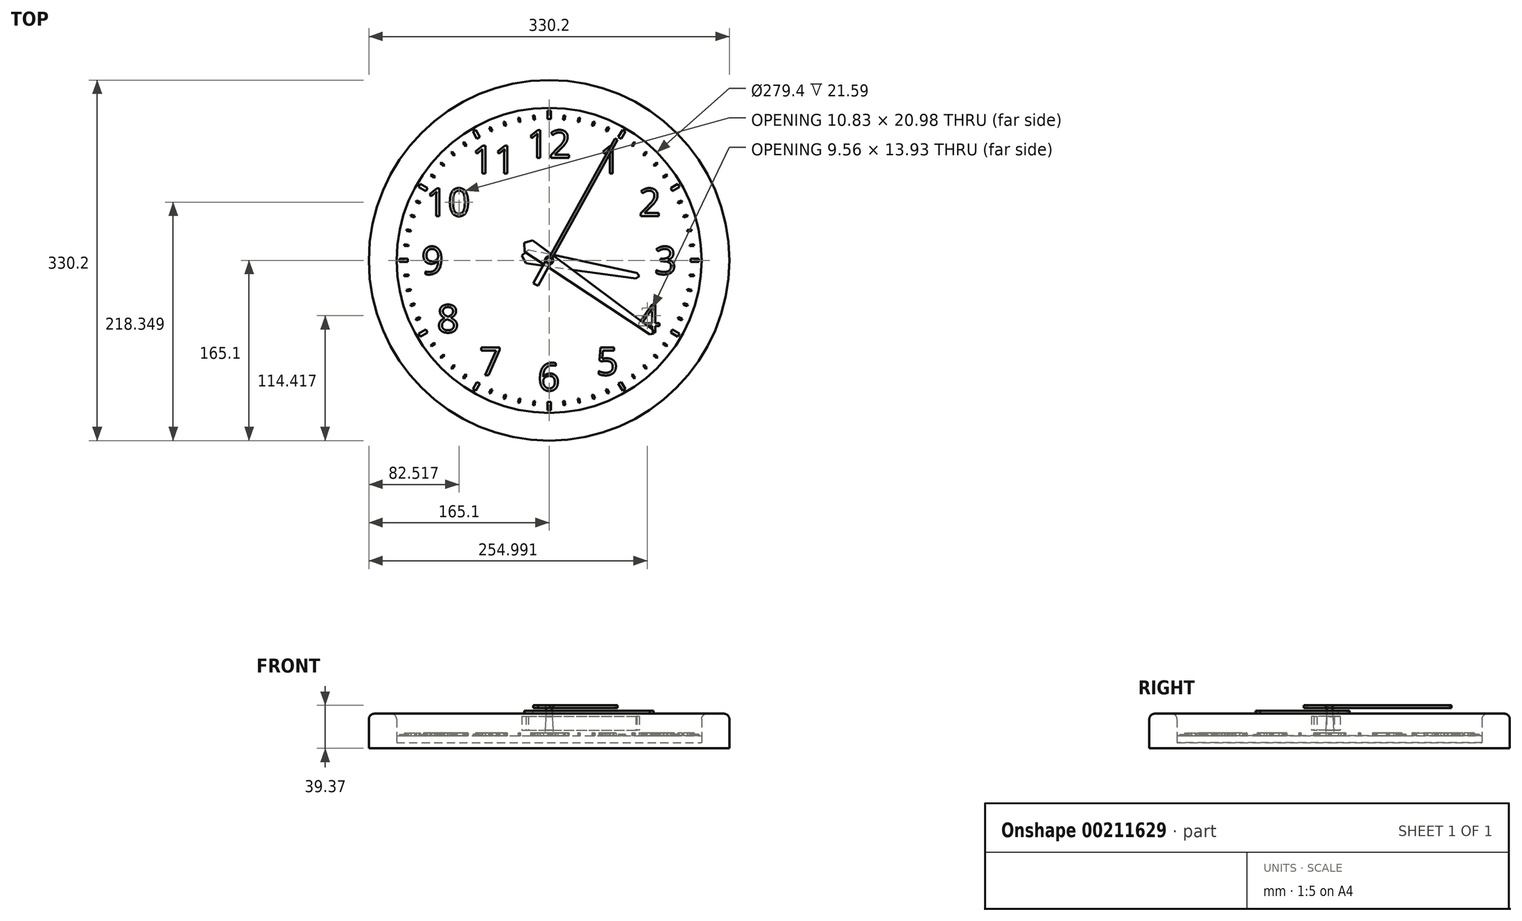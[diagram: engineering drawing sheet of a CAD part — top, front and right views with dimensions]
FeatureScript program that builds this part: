
annotation { "Feature Type Name" : "Feature", "Feature Type Description" : "" }
export const myFeature = defineFeature(function(context is Context, id is Id, definition is map)
    precondition{}
    {
        {
            var Q0;
            Q0=qCreatedBy(makeId("Front.planeOp"),FACE);
            var sketch = newSketch(context, id + "F0", { "sketchPlane" : qUnion([Q0])});
            skLineSegment(sketch, "E0", {"start": v(0, 0) * mm, "end": v(0, 54.8) * mm, "construction": true});
            skLineSegment(sketch, "E1.bottom", {"start": v(139.7, 0) * mm, "end": v(165.1, 0) * mm});
            skLineSegment(sketch, "E1.top", {"start": v(139.7, 31.75) * mm, "end": v(165.1, 31.75) * mm});
            skLineSegment(sketch, "E1.left", {"start": v(139.7, 5.08) * mm, "end": v(139.7, 31.75) * mm});
            skLineSegment(sketch, "E1.right", {"start": v(165.1, 0) * mm, "end": v(165.1, 31.75) * mm});
            skLineSegment(sketch, "E2", {"start": v(152.4, 0) * mm, "end": v(152.4, 31.75) * mm, "construction": true});
            skLineSegment(sketch, "E3.bottom", {"start": v(0, 0) * mm, "end": v(139.7, 0) * mm});
            skLineSegment(sketch, "E3.top", {"start": v(0, 5.08) * mm, "end": v(139.7, 5.08) * mm});
            skLineSegment(sketch, "E3.left", {"start": v(0, 0) * mm, "end": v(0, 5.08) * mm});
            skSolve(sketch);
        }
        {
            var Q0;
            Q0=makeQuery(id+"F0.imprint","IMPRINT",FACE,{"disambiguationData":[TD([[makeQuery(id+"F0.imprint","IMPRINT",EDGE,{"derivedFrom":sQuery(id+"F0.wireOp",EDGE,"E1.bottom")}),1.0]])]});
            var Q1;
            Q1=sQuery(id+"F0.wireOp",EDGE,"E0");
            revolve(context, id + "F1", {"entities" : qUnion([Q0]), "axis" : qUnion([Q1]), "revolveType" : RevolveType.FULL});
        }
        {
            var Q0;
            Q0=makeQuery(id+"F1.opRevolve","SWEPT_EDGE",EDGE,{"disambiguationData":[OSD([sQuery(id+"F0.wireOp",EDGE,"E1.top"),sQuery(id+"F0.wireOp",EDGE,"E1.left")])]});
            var Q1;
            Q1=makeQuery(id+"F1.opRevolve","SWEPT_EDGE",EDGE,{"disambiguationData":[OSD([sQuery(id+"F0.wireOp",EDGE,"E1.top"),sQuery(id+"F0.wireOp",EDGE,"E1.right")])]});
            fillet(context, id + "F2", {"entities" : qUnion([Q0, Q1]), "radius" : 5.08 * mm, "tangentPropagation" : true, "allowEdgeOverflow" : false});
        }
        {
            var Q0;
            Q0=makeQuery(id+"F1.opRevolve","SWEPT_FACE",FACE,{"disambiguationData":[OSD([sQuery(id+"F0.wireOp",EDGE,"E3.top")])]});
            extrude(context, id + "F3", {"entities" : qUnion([Q0]), "depth" : 6.35 * mm});
        }
        {
            var Q0;
            Q0=makeQuery(id+"F3.opExtrude","CAP_FACE",FACE,{"disambiguationData":[OSD([sQuery(id+"F0.wireOp",EDGE,"E3.top")])],"isStart":false});
            var sketch = newSketch(context, id + "F4", { "sketchPlane" : qUnion([Q0])});
            skText(sketch, "E4", { "text": "12", "fontName": "OpenSans-Regular.ttf"});
            skLineSegment(sketch, "E5", {"start": v(0, 0) * mm, "end": v(0, 106.68) * mm, "construction": true});
            skLineSegment(sketch, "E6.1.0", {"start": v(0, 0) * mm, "end": v(-53.34, 92.39) * mm, "construction": true});
            skLineSegment(sketch, "E6.2.0", {"start": v(0, 0) * mm, "end": v(-92.39, 53.34) * mm, "construction": true});
            skLineSegment(sketch, "E6.3.0", {"start": v(0, 0) * mm, "end": v(-106.68, 0) * mm, "construction": true});
            skLineSegment(sketch, "E6.4.0", {"start": v(0, 0) * mm, "end": v(-92.39, -53.34) * mm, "construction": true});
            skLineSegment(sketch, "E6.5.0", {"start": v(0, 0) * mm, "end": v(-53.34, -92.39) * mm, "construction": true});
            skLineSegment(sketch, "E6.6.0", {"start": v(0, 0) * mm, "end": v(0, -106.68) * mm, "construction": true});
            skLineSegment(sketch, "E6.7.0", {"start": v(0, 0) * mm, "end": v(53.34, -92.39) * mm, "construction": true});
            skLineSegment(sketch, "E6.8.0", {"start": v(0, 0) * mm, "end": v(92.39, -53.34) * mm, "construction": true});
            skLineSegment(sketch, "E6.9.0", {"start": v(0, 0) * mm, "end": v(106.68, 0) * mm, "construction": true});
            skLineSegment(sketch, "E6.10.0", {"start": v(0, 0) * mm, "end": v(92.39, 53.34) * mm, "construction": true});
            skLineSegment(sketch, "E6.11.0", {"start": v(0, 0) * mm, "end": v(53.34, 92.39) * mm, "construction": true});
            skPoint(sketch, "E6.center", {"position": v(0, 0) * mm});
            skText(sketch, "E7", { "text": "2", "fontName": "OpenSans-Regular.ttf"});
            skText(sketch, "E8", { "text": "3", "fontName": "OpenSans-Regular.ttf"});
            skText(sketch, "E9", { "text": "4", "fontName": "OpenSans-Regular.ttf"});
            skText(sketch, "E10", { "text": "1", "fontName": "OpenSans-Regular.ttf"});
            skText(sketch, "E11", { "text": "5", "fontName": "OpenSans-Regular.ttf"});
            skText(sketch, "E12", { "text": "6", "fontName": "OpenSans-Regular.ttf"});
            skText(sketch, "E13", { "text": "7", "fontName": "OpenSans-Regular.ttf"});
            skText(sketch, "E14", { "text": "9", "fontName": "OpenSans-Regular.ttf"});
            skText(sketch, "E15", { "text": "8", "fontName": "OpenSans-Regular.ttf"});
            skText(sketch, "E16", { "text": "10", "fontName": "OpenSans-Regular.ttf"});
            skText(sketch, "E17", { "text": "11", "fontName": "OpenSans-Regular.ttf"});
            const initialGuessF4  = {"E4": [-0.02037, 0.09398, 1, 0, 0.0254], "E7": [0.0821, 0.04064, 1, 0, 0.0254], "E8": [0.09649, -0.0127, 1, 0, 0.0254], "E9": [0.08151, -0.06604, 1, 0, 0.0254], "E10": [0.04604, 0.07969, 1, 0, 0.0254], "E11": [0.04313, -0.10509, 1, 0, 0.0254], "E12": [-0.01037, -0.11938, 1, 0, 0.0254], "E13": [-0.06367, -0.10509, 1, 0, 0.0254], "E14": [-0.11696, -0.0127, 1, 0, 0.0254], "E15": [-0.1027, -0.06604, 1, 0, 0.0254], "E16": [-0.11282, 0.04064, 1, 0, 0.0254], "E17": [-0.07073, 0.07969, 1, 0, 0.0254]};
            skSetInitialGuess(sketch, initialGuessF4);
            skSolve(sketch);
        }
        {
            var Q0;
            Q0=qSketchRegion(id+"F4",true);
            extrude(context, id + "F5", {"entities" : qUnion([Q0]), "depth" : 2.54 * mm});
        }
        {
            var Q0;
            Q0=makeQuery(id+"F3.opExtrude","CAP_FACE",FACE,{"disambiguationData":[OSD([sQuery(id+"F0.wireOp",EDGE,"E3.top")])],"isStart":false});
            cPlane(context, id + "F6", {"entities" : qUnion([Q0]), "cplaneType" : CPlaneType.OFFSET, "offset" : 5.08 * mm, "width" : 152.4 * mm, "height" : 152.4 * mm});
        }
        {
            var Q0;
            Q0=qCreatedBy(id+"F6.planeOp",FACE);
            var sketch = newSketch(context, id + "F7", { "sketchPlane" : qUnion([Q0])});
            skLineSegment(sketch, "E18", {"start": v(5, -0.88) * mm, "end": v(80.05, -14.11) * mm, "construction": true});
            skLineSegment(sketch, "E19", {"start": v(80.05, -14.11) * mm, "end": v(79.6, -16.62) * mm, "construction": true});
            skLineSegment(sketch, "E20", {"start": v(-20.01, 3.53) * mm, "end": v(-21.11, -2.72) * mm, "construction": true});
            skLineSegment(sketch, "E21", {"start": v(5, -0.88) * mm, "end": v(-25.01, 4.41) * mm, "construction": true});
            skLineSegment(sketch, "E22", {"start": v(-25.01, 4.41) * mm, "end": v(-21.11, -2.72) * mm});
            skLineSegment(sketch, "E23", {"start": v(-21.11, -2.72) * mm, "end": v(79.6, -16.62) * mm});
            skLineSegment(sketch, "E24", {"start": v(80.05, -14.11) * mm, "end": v(82.55, -14.56) * mm, "construction": true});
            skLineSegment(sketch, "E25", {"start": v(82.55, -14.56) * mm, "end": v(79.6, -16.62) * mm});
            skLineSegment(sketch, "E26.MirrorCS", {"start": v(82.55, -14.56) * mm, "end": v(80.49, -11.61) * mm});
            skLineSegment(sketch, "E27.MirrorCS", {"start": v(-18.9, 9.78) * mm, "end": v(80.49, -11.61) * mm});
            skLineSegment(sketch, "E28.MirrorCS", {"start": v(-25.01, 4.41) * mm, "end": v(-18.9, 9.78) * mm});
            skSolve(sketch);
        }
        {
            var Q0;
            Q0=makeQuery(id+"F7.imprint","IMPRINT",FACE,{"disambiguationData":[TD([[makeQuery(id+"F7.imprint","IMPRINT",EDGE,{"derivedFrom":sQuery(id+"F7.wireOp",EDGE,"E22")}),1.0]])]});
            extrude(context, id + "F8", {"entities" : qUnion([Q0]), "depth" : 12.7 * mm});
        }
        {
            var Q0;
            Q0=makeQuery(id+"F8.opExtrude","CAP_FACE",FACE,{"disambiguationData":[OSD([sQuery(id+"F7.wireOp",EDGE,"E22"),sQuery(id+"F7.wireOp",EDGE,"E23"),sQuery(id+"F7.wireOp",EDGE,"E25"),sQuery(id+"F7.wireOp",EDGE,"E26.MirrorCS"),sQuery(id+"F7.wireOp",EDGE,"E27.MirrorCS"),sQuery(id+"F7.wireOp",EDGE,"E28.MirrorCS")])],"isStart":false});
            cPlane(context, id + "F9", {"entities" : qUnion([Q0]), "cplaneType" : CPlaneType.OFFSET, "offset" : 2.54 * mm, "width" : 152.4 * mm, "height" : 152.4 * mm});
        }
        {
            var Q0;
            Q0=qCreatedBy(id+"F9.planeOp",FACE);
            var sketch = newSketch(context, id + "F10", { "sketchPlane" : qUnion([Q0])});
            skLineSegment(sketch, "E29", {"start": v(0, 0) * mm, "end": v(95.7, -67.02) * mm, "construction": true});
            skLineSegment(sketch, "E30", {"start": v(0, 0) * mm, "end": v(-22.89, 16.03) * mm, "construction": true});
            skLineSegment(sketch, "E31", {"start": v(-18.73, 13.11) * mm, "end": v(-15.08, 18.31) * mm, "construction": true});
            skLineSegment(sketch, "E32", {"start": v(93.63, -65.56) * mm, "end": v(95.09, -63.48) * mm, "construction": true});
            skLineSegment(sketch, "E33", {"start": v(-22.89, 16.03) * mm, "end": v(-15.08, 18.31) * mm});
            skLineSegment(sketch, "E34", {"start": v(-15.08, 18.31) * mm, "end": v(95.09, -63.48) * mm});
            skLineSegment(sketch, "E35", {"start": v(95.09, -63.48) * mm, "end": v(95.7, -67.02) * mm});
            skLineSegment(sketch, "E36.MirrorCS", {"start": v(-22.89, 16.03) * mm, "end": v(-22.37, 7.91) * mm});
            skLineSegment(sketch, "E37.MirrorCS", {"start": v(-22.37, 7.91) * mm, "end": v(92.17, -67.64) * mm});
            skLineSegment(sketch, "E38.MirrorCS", {"start": v(92.17, -67.64) * mm, "end": v(95.7, -67.02) * mm});
            skLineSegment(sketch, "E39", {"start": v(0, 0) * mm, "end": v(0, -35.35) * mm, "construction": true});
            skSolve(sketch);
        }
        {
            var Q0;
            Q0=makeQuery(id+"F10.imprint","IMPRINT",FACE,{"disambiguationData":[TD([[makeQuery(id+"F10.imprint","IMPRINT",EDGE,{"derivedFrom":sQuery(id+"F10.wireOp",EDGE,"E33")}),-1.0]])]});
            extrude(context, id + "F11", {"entities" : qUnion([Q0]), "depth" : 2.54 * mm});
        }
        {
            var Q0;
            Q0=makeQuery(id+"F11.opExtrude","CAP_FACE",FACE,{"disambiguationData":[OSD([sQuery(id+"F10.wireOp",EDGE,"E33"),sQuery(id+"F10.wireOp",EDGE,"E34"),sQuery(id+"F10.wireOp",EDGE,"E35"),sQuery(id+"F10.wireOp",EDGE,"E36.MirrorCS"),sQuery(id+"F10.wireOp",EDGE,"E37.MirrorCS"),sQuery(id+"F10.wireOp",EDGE,"E38.MirrorCS")])],"isStart":false});
            cPlane(context, id + "F12", {"entities" : qUnion([Q0]), "cplaneType" : CPlaneType.OFFSET, "offset" : 2.54 * mm, "width" : 152.4 * mm, "height" : 152.4 * mm});
        }
        {
            var Q0;
            Q0=qCreatedBy(id+"F12.planeOp",FACE);
            var sketch = newSketch(context, id + "F13", { "sketchPlane" : qUnion([Q0])});
            skArc(sketch, "E40", {"start": v(0.85, -3.72) * mm, "mid": v(3.63, -1.17) * mm, "end": v(2.85, 2.53) * mm});
            skLineSegment(sketch, "E41", {"start": v(0, 0) * mm, "end": v(61.55, 111.09) * mm, "construction": true});
            skLineSegment(sketch, "E42", {"start": v(0, 0) * mm, "end": v(-12.31, -22.22) * mm, "construction": true});
            skLineSegment(sketch, "E43", {"start": v(-12.31, -22.22) * mm, "end": v(-10.09, -23.45) * mm});
            skLineSegment(sketch, "E44", {"start": v(-10.09, -23.45) * mm, "end": v(0.85, -3.72) * mm});
            skLineSegment(sketch, "E45", {"start": v(61.55, 111.09) * mm, "end": v(62.66, 110.47) * mm});
            skLineSegment(sketch, "E46", {"start": v(62.66, 110.47) * mm, "end": v(2.85, 2.53) * mm});
            skLineSegment(sketch, "E47.MirrorCS", {"start": v(61.55, 111.09) * mm, "end": v(60.44, 111.7) * mm});
            skLineSegment(sketch, "E48.MirrorCS", {"start": v(60.44, 111.7) * mm, "end": v(0.63, 3.76) * mm});
            skArc(sketch, "E49.MirrorCS", {"start": v(-3.6, -1.25) * mm, "mid": v(-2.91, 2.46) * mm, "end": v(0.63, 3.76) * mm});
            skLineSegment(sketch, "E50.MirrorCS", {"start": v(-14.53, -20.99) * mm, "end": v(-3.6, -1.25) * mm});
            skLineSegment(sketch, "E51.MirrorCS", {"start": v(-12.31, -22.22) * mm, "end": v(-14.53, -20.99) * mm});
            skSolve(sketch);
        }
        {
            var Q0;
            Q0=makeQuery(id+"F13.imprint","IMPRINT",FACE,{"disambiguationData":[TD([[makeQuery(id+"F13.imprint","IMPRINT",EDGE,{"derivedFrom":sQuery(id+"F13.wireOp",EDGE,"E40")}),1.0]])]});
            extrude(context, id + "F14", {"entities" : qUnion([Q0]), "depth" : 2.54 * mm});
        }
        {
            var Q0;
            Q0=makeQuery(id+"F3.opExtrude","CAP_FACE",FACE,{"disambiguationData":[OSD([sQuery(id+"F0.wireOp",EDGE,"E3.top")])],"isStart":false});
            var sketch = newSketch(context, id + "F15", { "sketchPlane" : qUnion([Q0])});
            skCircle(sketch, "E52", {"center": v(0, 0) * mm, "radius": 3.81 * mm});
            skSolve(sketch);
        }
        {
            var Q0;
            Q0=makeQuery(id+"F14.opExtrude","CAP_FACE",FACE,{"disambiguationData":[OSD([sQuery(id+"F13.wireOp",EDGE,"E40"),sQuery(id+"F13.wireOp",EDGE,"E43"),sQuery(id+"F13.wireOp",EDGE,"E44"),sQuery(id+"F13.wireOp",EDGE,"E45"),sQuery(id+"F13.wireOp",EDGE,"E46"),sQuery(id+"F13.wireOp",EDGE,"E47.MirrorCS"),sQuery(id+"F13.wireOp",EDGE,"E48.MirrorCS"),sQuery(id+"F13.wireOp",EDGE,"E49.MirrorCS"),sQuery(id+"F13.wireOp",EDGE,"E50.MirrorCS"),sQuery(id+"F13.wireOp",EDGE,"E51.MirrorCS")])],"isStart":false});
            var sketch = newSketch(context, id + "F16", { "sketchPlane" : qUnion([Q0])});
            skCircle(sketch, "E53", {"center": v(0, 0) * mm, "radius": 2.54 * mm});
            skSolve(sketch);
        }
        {
            var Q1;
            Q1=makeQuery(id+"F15.imprint","IMPRINT",FACE,{"disambiguationData":[TD([[makeQuery(id+"F15.imprint","IMPRINT",EDGE,{"derivedFrom":sQuery(id+"F15.wireOp",EDGE,"E52")}),1.0]])]});
            var Q2;
            Q2=makeQuery(id+"F16.imprint","IMPRINT",FACE,{"disambiguationData":[TD([[makeQuery(id+"F16.imprint","IMPRINT",EDGE,{"derivedFrom":sQuery(id+"F16.wireOp",EDGE,"E53")}),1.0]])]});
            loft(context, id + "F17", {"sheetProfilesArray" : [{ "sheetProfileEntities" : qUnion([Q1]) }, { "sheetProfileEntities" : qUnion([Q2]) }]});
        }
        {
            var Q0;
            Q0=makeQuery(id+"F17.opLoft","SWEPT_BODY",BODY,{"disambiguationData":[OSD([makeQuery(id+"F15.imprint","IMPRINT",FACE,{"disambiguationData":[TD([[makeQuery(id+"F15.imprint","IMPRINT",EDGE,{"derivedFrom":sQuery(id+"F15.wireOp",EDGE,"E52")}),1.0]])]}),makeQuery(id+"F16.imprint","IMPRINT",FACE,{"disambiguationData":[TD([[makeQuery(id+"F16.imprint","IMPRINT",EDGE,{"derivedFrom":sQuery(id+"F16.wireOp",EDGE,"E53")}),1.0]])]})])]});
            var Q1;
            Q1=makeQuery(id+"F8.opExtrude","SWEPT_BODY",BODY,{"disambiguationData":[OSD([sQuery(id+"F7.wireOp",EDGE,"E22"),sQuery(id+"F7.wireOp",EDGE,"E23"),sQuery(id+"F7.wireOp",EDGE,"E25"),sQuery(id+"F7.wireOp",EDGE,"E26.MirrorCS"),sQuery(id+"F7.wireOp",EDGE,"E27.MirrorCS"),sQuery(id+"F7.wireOp",EDGE,"E28.MirrorCS")])]});
            booleanBodies(context, id + "F18", {"operationType" : BooleanOperationType.SUBTRACTION, "tools" : qUnion([Q0]), "targets" : qUnion([Q1]), "keepTools" : true});
        }
        {
            var Q0;
            Q0=makeQuery(id+"F17.opLoft","SWEPT_BODY",BODY,{"disambiguationData":[OSD([makeQuery(id+"F15.imprint","IMPRINT",FACE,{"disambiguationData":[TD([[makeQuery(id+"F15.imprint","IMPRINT",EDGE,{"derivedFrom":sQuery(id+"F15.wireOp",EDGE,"E52")}),1.0]])]}),makeQuery(id+"F16.imprint","IMPRINT",FACE,{"disambiguationData":[TD([[makeQuery(id+"F16.imprint","IMPRINT",EDGE,{"derivedFrom":sQuery(id+"F16.wireOp",EDGE,"E53")}),1.0]])]})])]});
            var Q1;
            Q1=makeQuery(id+"F11.opExtrude","SWEPT_BODY",BODY,{"disambiguationData":[OSD([sQuery(id+"F10.wireOp",EDGE,"E33"),sQuery(id+"F10.wireOp",EDGE,"E34"),sQuery(id+"F10.wireOp",EDGE,"E35"),sQuery(id+"F10.wireOp",EDGE,"E36.MirrorCS"),sQuery(id+"F10.wireOp",EDGE,"E37.MirrorCS"),sQuery(id+"F10.wireOp",EDGE,"E38.MirrorCS")])]});
            booleanBodies(context, id + "F19", {"operationType" : BooleanOperationType.SUBTRACTION, "tools" : qUnion([Q0]), "targets" : qUnion([Q1]), "keepTools" : true});
        }
        {
            var Q0;
            Q0=makeQuery(id+"F17.opLoft","SWEPT_BODY",BODY,{"disambiguationData":[OSD([makeQuery(id+"F15.imprint","IMPRINT",FACE,{"disambiguationData":[TD([[makeQuery(id+"F15.imprint","IMPRINT",EDGE,{"derivedFrom":sQuery(id+"F15.wireOp",EDGE,"E52")}),1.0]])]}),makeQuery(id+"F16.imprint","IMPRINT",FACE,{"disambiguationData":[TD([[makeQuery(id+"F16.imprint","IMPRINT",EDGE,{"derivedFrom":sQuery(id+"F16.wireOp",EDGE,"E53")}),1.0]])]})])]});
            var Q1;
            Q1=makeQuery(id+"F14.opExtrude","SWEPT_BODY",BODY,{"disambiguationData":[OSD([sQuery(id+"F13.wireOp",EDGE,"E40"),sQuery(id+"F13.wireOp",EDGE,"E43"),sQuery(id+"F13.wireOp",EDGE,"E44"),sQuery(id+"F13.wireOp",EDGE,"E45"),sQuery(id+"F13.wireOp",EDGE,"E46"),sQuery(id+"F13.wireOp",EDGE,"E47.MirrorCS"),sQuery(id+"F13.wireOp",EDGE,"E48.MirrorCS"),sQuery(id+"F13.wireOp",EDGE,"E49.MirrorCS"),sQuery(id+"F13.wireOp",EDGE,"E50.MirrorCS"),sQuery(id+"F13.wireOp",EDGE,"E51.MirrorCS")])]});
            booleanBodies(context, id + "F20", {"operationType" : BooleanOperationType.SUBTRACTION, "tools" : qUnion([Q0]), "targets" : qUnion([Q1]), "keepTools" : true});
        }
        {
            var Q0;
            Q0=makeQuery(id+"F18.opBoolean","INTERSECT",EDGE,{"derivedFrom":[makeQuery(id+"F17.opLoft","SWEPT_FACE",FACE,{"disambiguationData":[OSD([sQuery(id+"F15.wireOp",EDGE,"E52"),sQuery(id+"F16.wireOp",EDGE,"E53")])]}),makeQuery(id+"F8.opExtrude","CAP_FACE",FACE,{"disambiguationData":[OSD([sQuery(id+"F7.wireOp",EDGE,"E22"),sQuery(id+"F7.wireOp",EDGE,"E23"),sQuery(id+"F7.wireOp",EDGE,"E25"),sQuery(id+"F7.wireOp",EDGE,"E26.MirrorCS"),sQuery(id+"F7.wireOp",EDGE,"E27.MirrorCS"),sQuery(id+"F7.wireOp",EDGE,"E28.MirrorCS")])],"isStart":true})]});
            var Q1;
            Q1=makeQuery(id+"F18.opBoolean","INTERSECT",EDGE,{"derivedFrom":[makeQuery(id+"F17.opLoft","SWEPT_FACE",FACE,{"disambiguationData":[OSD([sQuery(id+"F15.wireOp",EDGE,"E52"),sQuery(id+"F16.wireOp",EDGE,"E53")])]}),makeQuery(id+"F8.opExtrude","CAP_FACE",FACE,{"disambiguationData":[OSD([sQuery(id+"F7.wireOp",EDGE,"E22"),sQuery(id+"F7.wireOp",EDGE,"E23"),sQuery(id+"F7.wireOp",EDGE,"E25"),sQuery(id+"F7.wireOp",EDGE,"E26.MirrorCS"),sQuery(id+"F7.wireOp",EDGE,"E27.MirrorCS"),sQuery(id+"F7.wireOp",EDGE,"E28.MirrorCS")])],"isStart":false})]});
            var Q2;
            Q2=makeQuery(id+"F19.opBoolean","INTERSECT",EDGE,{"derivedFrom":[makeQuery(id+"F17.opLoft","SWEPT_FACE",FACE,{"disambiguationData":[OSD([sQuery(id+"F15.wireOp",EDGE,"E52"),sQuery(id+"F16.wireOp",EDGE,"E53")])]}),makeQuery(id+"F11.opExtrude","CAP_FACE",FACE,{"disambiguationData":[OSD([sQuery(id+"F10.wireOp",EDGE,"E33"),sQuery(id+"F10.wireOp",EDGE,"E34"),sQuery(id+"F10.wireOp",EDGE,"E35"),sQuery(id+"F10.wireOp",EDGE,"E36.MirrorCS"),sQuery(id+"F10.wireOp",EDGE,"E37.MirrorCS"),sQuery(id+"F10.wireOp",EDGE,"E38.MirrorCS")])],"isStart":true})]});
            var Q3;
            Q3=makeQuery(id+"F19.opBoolean","INTERSECT",EDGE,{"derivedFrom":[makeQuery(id+"F17.opLoft","SWEPT_FACE",FACE,{"disambiguationData":[OSD([sQuery(id+"F15.wireOp",EDGE,"E52"),sQuery(id+"F16.wireOp",EDGE,"E53")])]}),makeQuery(id+"F11.opExtrude","CAP_FACE",FACE,{"disambiguationData":[OSD([sQuery(id+"F10.wireOp",EDGE,"E33"),sQuery(id+"F10.wireOp",EDGE,"E34"),sQuery(id+"F10.wireOp",EDGE,"E35"),sQuery(id+"F10.wireOp",EDGE,"E36.MirrorCS"),sQuery(id+"F10.wireOp",EDGE,"E37.MirrorCS"),sQuery(id+"F10.wireOp",EDGE,"E38.MirrorCS")])],"isStart":false})]});
            var Q4;
            Q4=makeQuery(id+"F20.opBoolean","INTERSECT",EDGE,{"derivedFrom":[makeQuery(id+"F17.opLoft","SWEPT_FACE",FACE,{"disambiguationData":[OSD([sQuery(id+"F15.wireOp",EDGE,"E52"),sQuery(id+"F16.wireOp",EDGE,"E53")])]}),makeQuery(id+"F14.opExtrude","CAP_FACE",FACE,{"disambiguationData":[OSD([sQuery(id+"F13.wireOp",EDGE,"E40"),sQuery(id+"F13.wireOp",EDGE,"E43"),sQuery(id+"F13.wireOp",EDGE,"E44"),sQuery(id+"F13.wireOp",EDGE,"E45"),sQuery(id+"F13.wireOp",EDGE,"E46"),sQuery(id+"F13.wireOp",EDGE,"E47.MirrorCS"),sQuery(id+"F13.wireOp",EDGE,"E48.MirrorCS"),sQuery(id+"F13.wireOp",EDGE,"E49.MirrorCS"),sQuery(id+"F13.wireOp",EDGE,"E50.MirrorCS"),sQuery(id+"F13.wireOp",EDGE,"E51.MirrorCS")])],"isStart":true})]});
            var Q5;
            Q5=makeQuery(id+"F20.opBoolean","COPY",EDGE,{"derivedFrom":makeQuery(id+"F17.opLoft","MID_CAP_EDGE",EDGE,{"disambiguationData":[OSD([sQuery(id+"F15.wireOp",EDGE,"E52"),sQuery(id+"F16.wireOp",EDGE,"E53")])],"capPos":1.0})});
            chamfer(context, id + "F21", {"entities" : qUnion([Q0, Q1, Q2, Q3, Q4, Q5]), "width" : 0.25 * mm, "tangentPropagation" : true});
        }
        {
            var Q0;
            Q0=makeQuery(id+"F3.opExtrude","CAP_FACE",FACE,{"disambiguationData":[OSD([sQuery(id+"F0.wireOp",EDGE,"E3.top")])],"isStart":false});
            var sketch = newSketch(context, id + "F22", { "sketchPlane" : qUnion([Q0])});
            skLineSegment(sketch, "E54", {"start": v(0, 0) * mm, "end": v(0, 139.7) * mm, "construction": true});
            skLineSegment(sketch, "E55.bottom", {"start": v(1.52, 137.16) * mm, "end": v(-1.52, 137.16) * mm});
            skLineSegment(sketch, "E55.top", {"start": v(1.52, 129.54) * mm, "end": v(-1.52, 129.54) * mm});
            skLineSegment(sketch, "E55.left", {"start": v(1.52, 137.16) * mm, "end": v(1.52, 129.54) * mm});
            skLineSegment(sketch, "E55.right", {"start": v(-1.52, 137.16) * mm, "end": v(-1.52, 129.54) * mm});
            skPoint(sketch, "E55.middle", {"position": v(0, 133.35) * mm});
            skSolve(sketch);
        }
        {
            var Q0;
            Q0=makeQuery(id+"F22.imprint","IMPRINT",FACE,{"disambiguationData":[TD([[makeQuery(id+"F22.imprint","IMPRINT",EDGE,{"derivedFrom":sQuery(id+"F22.wireOp",EDGE,"E55.bottom")}),1.0]])]});
            extrude(context, id + "F23", {"entities" : qUnion([Q0]), "depth" : 1.27 * mm});
        }
        {
            var Q0;
            Q0=makeQuery(id+"F23.opExtrude","SWEPT_BODY",BODY,{"disambiguationData":[OSD([sQuery(id+"F22.wireOp",EDGE,"E55.bottom"),sQuery(id+"F22.wireOp",EDGE,"E55.top"),sQuery(id+"F22.wireOp",EDGE,"E55.left"),sQuery(id+"F22.wireOp",EDGE,"E55.right")])]});
            var Q1;
            Q1=sQuery(id+"F0.wireOp",EDGE,"E0");
            circularPattern(context, id + "F24", {"entities" : qUnion([Q0]), "axis" : qUnion([Q1]), "angle" : 360 * degree, "instanceCount" : 12, "equalSpace" : true});
        }
        {
            var Q0;
            Q0=makeQuery(id+"F3.opExtrude","CAP_FACE",FACE,{"disambiguationData":[OSD([sQuery(id+"F0.wireOp",EDGE,"E3.top")])],"isStart":false});
            var sketch = newSketch(context, id + "F25", { "sketchPlane" : qUnion([Q0])});
            skLineSegment(sketch, "E56", {"start": v(0, 0) * mm, "end": v(0, 65.46) * mm, "construction": true});
            skLineSegment(sketch, "E57", {"start": v(0, 0) * mm, "end": v(13.94, 132.62) * mm, "construction": true});
            skLineSegment(sketch, "E58", {"start": v(13.54, 128.83) * mm, "end": v(14.3, 128.75) * mm});
            skLineSegment(sketch, "E59", {"start": v(13.94, 132.62) * mm, "end": v(14.7, 132.54) * mm});
            skLineSegment(sketch, "E60", {"start": v(14.7, 132.54) * mm, "end": v(14.3, 128.75) * mm});
            skLineSegment(sketch, "E61.MirrorCS", {"start": v(13.94, 132.62) * mm, "end": v(13.18, 132.7) * mm});
            skLineSegment(sketch, "E62.MirrorCS", {"start": v(13.18, 132.7) * mm, "end": v(12.78, 128.91) * mm});
            skLineSegment(sketch, "E63.MirrorCS", {"start": v(13.54, 128.83) * mm, "end": v(12.78, 128.91) * mm});
            skLineSegment(sketch, "E64.2.0", {"start": v(-13.18, 132.7) * mm, "end": v(-12.78, 128.91) * mm});
            skLineSegment(sketch, "E64.2.1", {"start": v(-13.94, 132.62) * mm, "end": v(-13.18, 132.7) * mm});
            skLineSegment(sketch, "E64.2.2", {"start": v(-13.94, 132.62) * mm, "end": v(-14.7, 132.54) * mm});
            skLineSegment(sketch, "E64.2.3", {"start": v(-14.7, 132.54) * mm, "end": v(-14.3, 128.75) * mm});
            skLineSegment(sketch, "E64.2.4", {"start": v(-13.54, 128.83) * mm, "end": v(-14.3, 128.75) * mm});
            skLineSegment(sketch, "E64.2.5", {"start": v(-13.54, 128.83) * mm, "end": v(-12.78, 128.91) * mm});
            skLineSegment(sketch, "E64.3.0", {"start": v(-26.98, 130.6) * mm, "end": v(-26.19, 126.87) * mm});
            skLineSegment(sketch, "E64.3.1", {"start": v(-27.73, 130.44) * mm, "end": v(-26.98, 130.6) * mm});
            skLineSegment(sketch, "E64.3.2", {"start": v(-27.73, 130.44) * mm, "end": v(-28.47, 130.28) * mm});
            skLineSegment(sketch, "E64.3.3", {"start": v(-28.47, 130.28) * mm, "end": v(-27.68, 126.55) * mm});
            skLineSegment(sketch, "E64.3.4", {"start": v(-26.93, 126.7) * mm, "end": v(-27.68, 126.55) * mm});
            skLineSegment(sketch, "E64.3.5", {"start": v(-26.93, 126.7) * mm, "end": v(-26.19, 126.87) * mm});
            skLineSegment(sketch, "E64.4.0", {"start": v(-40.48, 127.06) * mm, "end": v(-39.3, 123.44) * mm});
            skLineSegment(sketch, "E64.4.1", {"start": v(-41.2, 126.82) * mm, "end": v(-40.48, 127.06) * mm});
            skLineSegment(sketch, "E64.4.2", {"start": v(-41.2, 126.82) * mm, "end": v(-41.93, 126.59) * mm});
            skLineSegment(sketch, "E64.4.3", {"start": v(-41.93, 126.59) * mm, "end": v(-40.75, 122.96) * mm});
            skLineSegment(sketch, "E64.4.4", {"start": v(-40.03, 123.2) * mm, "end": v(-40.75, 122.96) * mm});
            skLineSegment(sketch, "E64.4.5", {"start": v(-40.03, 123.2) * mm, "end": v(-39.3, 123.44) * mm});
            skLineSegment(sketch, "E64.5.0", {"start": v(-53.54, 122.13) * mm, "end": v(-52, 118.65) * mm});
            skLineSegment(sketch, "E64.5.1", {"start": v(-54.24, 121.82) * mm, "end": v(-53.54, 122.13) * mm});
            skLineSegment(sketch, "E64.5.2", {"start": v(-54.24, 121.82) * mm, "end": v(-54.93, 121.51) * mm});
            skLineSegment(sketch, "E64.5.3", {"start": v(-54.93, 121.51) * mm, "end": v(-53.38, 118.03) * mm});
            skLineSegment(sketch, "E64.5.4", {"start": v(-52.69, 118.34) * mm, "end": v(-53.38, 118.03) * mm});
            skLineSegment(sketch, "E64.5.5", {"start": v(-52.69, 118.34) * mm, "end": v(-52, 118.65) * mm});
            skLineSegment(sketch, "E64.7.0", {"start": v(-77.76, 108.33) * mm, "end": v(-75.53, 105.25) * mm});
            skLineSegment(sketch, "E64.7.1", {"start": v(-78.38, 107.88) * mm, "end": v(-77.76, 108.33) * mm});
            skLineSegment(sketch, "E64.7.2", {"start": v(-78.38, 107.88) * mm, "end": v(-79, 107.43) * mm});
            skLineSegment(sketch, "E64.7.3", {"start": v(-79, 107.43) * mm, "end": v(-76.76, 104.35) * mm});
            skLineSegment(sketch, "E64.7.4", {"start": v(-76.14, 104.8) * mm, "end": v(-76.76, 104.35) * mm});
            skLineSegment(sketch, "E64.7.5", {"start": v(-76.14, 104.8) * mm, "end": v(-75.53, 105.25) * mm});
            skLineSegment(sketch, "E64.8.0", {"start": v(-88.66, 99.6) * mm, "end": v(-86.11, 96.78) * mm});
            skLineSegment(sketch, "E64.8.1", {"start": v(-89.23, 99.1) * mm, "end": v(-88.66, 99.6) * mm});
            skLineSegment(sketch, "E64.8.2", {"start": v(-89.23, 99.1) * mm, "end": v(-89.8, 98.59) * mm});
            skLineSegment(sketch, "E64.8.3", {"start": v(-89.8, 98.59) * mm, "end": v(-87.25, 95.76) * mm});
            skLineSegment(sketch, "E64.8.4", {"start": v(-86.68, 96.27) * mm, "end": v(-87.25, 95.76) * mm});
            skLineSegment(sketch, "E64.8.5", {"start": v(-86.68, 96.27) * mm, "end": v(-86.11, 96.78) * mm});
            skLineSegment(sketch, "E64.9.0", {"start": v(-98.59, 89.8) * mm, "end": v(-95.76, 87.25) * mm});
            skLineSegment(sketch, "E64.9.1", {"start": v(-99.1, 89.23) * mm, "end": v(-98.59, 89.8) * mm});
            skLineSegment(sketch, "E64.9.2", {"start": v(-99.1, 89.23) * mm, "end": v(-99.6, 88.66) * mm});
            skLineSegment(sketch, "E64.9.3", {"start": v(-99.6, 88.66) * mm, "end": v(-96.78, 86.11) * mm});
            skLineSegment(sketch, "E64.9.4", {"start": v(-96.27, 86.68) * mm, "end": v(-96.78, 86.11) * mm});
            skLineSegment(sketch, "E64.9.5", {"start": v(-96.27, 86.68) * mm, "end": v(-95.76, 87.25) * mm});
            skLineSegment(sketch, "E64.10.0", {"start": v(-107.43, 79) * mm, "end": v(-104.35, 76.76) * mm});
            skLineSegment(sketch, "E64.10.1", {"start": v(-107.88, 78.38) * mm, "end": v(-107.43, 79) * mm});
            skLineSegment(sketch, "E64.10.2", {"start": v(-107.88, 78.38) * mm, "end": v(-108.33, 77.76) * mm});
            skLineSegment(sketch, "E64.10.3", {"start": v(-108.33, 77.76) * mm, "end": v(-105.25, 75.53) * mm});
            skLineSegment(sketch, "E64.10.4", {"start": v(-104.8, 76.14) * mm, "end": v(-105.25, 75.53) * mm});
            skLineSegment(sketch, "E64.10.5", {"start": v(-104.8, 76.14) * mm, "end": v(-104.35, 76.76) * mm});
            skLineSegment(sketch, "E64.12.0", {"start": v(-121.51, 54.93) * mm, "end": v(-118.03, 53.38) * mm});
            skLineSegment(sketch, "E64.12.1", {"start": v(-121.82, 54.24) * mm, "end": v(-121.51, 54.93) * mm});
            skLineSegment(sketch, "E64.12.2", {"start": v(-121.82, 54.24) * mm, "end": v(-122.13, 53.54) * mm});
            skLineSegment(sketch, "E64.12.3", {"start": v(-122.13, 53.54) * mm, "end": v(-118.65, 52) * mm});
            skLineSegment(sketch, "E64.12.4", {"start": v(-118.34, 52.69) * mm, "end": v(-118.65, 52) * mm});
            skLineSegment(sketch, "E64.12.5", {"start": v(-118.34, 52.69) * mm, "end": v(-118.03, 53.38) * mm});
            skLineSegment(sketch, "E64.13.0", {"start": v(-126.59, 41.93) * mm, "end": v(-122.96, 40.75) * mm});
            skLineSegment(sketch, "E64.13.1", {"start": v(-126.82, 41.2) * mm, "end": v(-126.59, 41.93) * mm});
            skLineSegment(sketch, "E64.13.2", {"start": v(-126.82, 41.2) * mm, "end": v(-127.06, 40.48) * mm});
            skLineSegment(sketch, "E64.13.3", {"start": v(-127.06, 40.48) * mm, "end": v(-123.44, 39.3) * mm});
            skLineSegment(sketch, "E64.13.4", {"start": v(-123.2, 40.03) * mm, "end": v(-123.44, 39.3) * mm});
            skLineSegment(sketch, "E64.13.5", {"start": v(-123.2, 40.03) * mm, "end": v(-122.96, 40.75) * mm});
            skLineSegment(sketch, "E64.14.0", {"start": v(-130.28, 28.47) * mm, "end": v(-126.55, 27.68) * mm});
            skLineSegment(sketch, "E64.14.1", {"start": v(-130.44, 27.73) * mm, "end": v(-130.28, 28.47) * mm});
            skLineSegment(sketch, "E64.14.2", {"start": v(-130.44, 27.73) * mm, "end": v(-130.6, 26.98) * mm});
            skLineSegment(sketch, "E64.14.3", {"start": v(-130.6, 26.98) * mm, "end": v(-126.87, 26.19) * mm});
            skLineSegment(sketch, "E64.14.4", {"start": v(-126.7, 26.93) * mm, "end": v(-126.87, 26.19) * mm});
            skLineSegment(sketch, "E64.14.5", {"start": v(-126.7, 26.93) * mm, "end": v(-126.55, 27.68) * mm});
            skLineSegment(sketch, "E64.15.0", {"start": v(-132.54, 14.7) * mm, "end": v(-128.75, 14.3) * mm});
            skLineSegment(sketch, "E64.15.1", {"start": v(-132.62, 13.94) * mm, "end": v(-132.54, 14.7) * mm});
            skLineSegment(sketch, "E64.15.2", {"start": v(-132.62, 13.94) * mm, "end": v(-132.7, 13.18) * mm});
            skLineSegment(sketch, "E64.15.3", {"start": v(-132.7, 13.18) * mm, "end": v(-128.91, 12.78) * mm});
            skLineSegment(sketch, "E64.15.4", {"start": v(-128.83, 13.54) * mm, "end": v(-128.91, 12.78) * mm});
            skLineSegment(sketch, "E64.15.5", {"start": v(-128.83, 13.54) * mm, "end": v(-128.75, 14.3) * mm});
            skLineSegment(sketch, "E64.17.0", {"start": v(-132.7, -13.18) * mm, "end": v(-128.91, -12.78) * mm});
            skLineSegment(sketch, "E64.17.1", {"start": v(-132.62, -13.94) * mm, "end": v(-132.7, -13.18) * mm});
            skLineSegment(sketch, "E64.17.2", {"start": v(-132.62, -13.94) * mm, "end": v(-132.54, -14.7) * mm});
            skLineSegment(sketch, "E64.17.3", {"start": v(-132.54, -14.7) * mm, "end": v(-128.75, -14.3) * mm});
            skLineSegment(sketch, "E64.17.4", {"start": v(-128.83, -13.54) * mm, "end": v(-128.75, -14.3) * mm});
            skLineSegment(sketch, "E64.17.5", {"start": v(-128.83, -13.54) * mm, "end": v(-128.91, -12.78) * mm});
            skLineSegment(sketch, "E64.18.0", {"start": v(-130.6, -26.98) * mm, "end": v(-126.87, -26.19) * mm});
            skLineSegment(sketch, "E64.18.1", {"start": v(-130.44, -27.73) * mm, "end": v(-130.6, -26.98) * mm});
            skLineSegment(sketch, "E64.18.2", {"start": v(-130.44, -27.73) * mm, "end": v(-130.28, -28.47) * mm});
            skLineSegment(sketch, "E64.18.3", {"start": v(-130.28, -28.47) * mm, "end": v(-126.55, -27.68) * mm});
            skLineSegment(sketch, "E64.18.4", {"start": v(-126.7, -26.93) * mm, "end": v(-126.55, -27.68) * mm});
            skLineSegment(sketch, "E64.18.5", {"start": v(-126.7, -26.93) * mm, "end": v(-126.87, -26.19) * mm});
            skLineSegment(sketch, "E64.19.0", {"start": v(-127.06, -40.48) * mm, "end": v(-123.44, -39.3) * mm});
            skLineSegment(sketch, "E64.19.1", {"start": v(-126.82, -41.2) * mm, "end": v(-127.06, -40.48) * mm});
            skLineSegment(sketch, "E64.19.2", {"start": v(-126.82, -41.2) * mm, "end": v(-126.59, -41.93) * mm});
            skLineSegment(sketch, "E64.19.3", {"start": v(-126.59, -41.93) * mm, "end": v(-122.96, -40.75) * mm});
            skLineSegment(sketch, "E64.19.4", {"start": v(-123.2, -40.03) * mm, "end": v(-122.96, -40.75) * mm});
            skLineSegment(sketch, "E64.19.5", {"start": v(-123.2, -40.03) * mm, "end": v(-123.44, -39.3) * mm});
            skLineSegment(sketch, "E64.20.0", {"start": v(-122.13, -53.54) * mm, "end": v(-118.65, -52) * mm});
            skLineSegment(sketch, "E64.20.1", {"start": v(-121.82, -54.24) * mm, "end": v(-122.13, -53.54) * mm});
            skLineSegment(sketch, "E64.20.2", {"start": v(-121.82, -54.24) * mm, "end": v(-121.51, -54.93) * mm});
            skLineSegment(sketch, "E64.20.3", {"start": v(-121.51, -54.93) * mm, "end": v(-118.03, -53.38) * mm});
            skLineSegment(sketch, "E64.20.4", {"start": v(-118.34, -52.69) * mm, "end": v(-118.03, -53.38) * mm});
            skLineSegment(sketch, "E64.20.5", {"start": v(-118.34, -52.69) * mm, "end": v(-118.65, -52) * mm});
            skLineSegment(sketch, "E64.22.0", {"start": v(-108.33, -77.76) * mm, "end": v(-105.25, -75.53) * mm});
            skLineSegment(sketch, "E64.22.1", {"start": v(-107.88, -78.38) * mm, "end": v(-108.33, -77.76) * mm});
            skLineSegment(sketch, "E64.22.2", {"start": v(-107.88, -78.38) * mm, "end": v(-107.43, -79) * mm});
            skLineSegment(sketch, "E64.22.3", {"start": v(-107.43, -79) * mm, "end": v(-104.35, -76.76) * mm});
            skLineSegment(sketch, "E64.22.4", {"start": v(-104.8, -76.14) * mm, "end": v(-104.35, -76.76) * mm});
            skLineSegment(sketch, "E64.22.5", {"start": v(-104.8, -76.14) * mm, "end": v(-105.25, -75.53) * mm});
            skLineSegment(sketch, "E64.23.0", {"start": v(-99.6, -88.66) * mm, "end": v(-96.78, -86.11) * mm});
            skLineSegment(sketch, "E64.23.1", {"start": v(-99.1, -89.23) * mm, "end": v(-99.6, -88.66) * mm});
            skLineSegment(sketch, "E64.23.2", {"start": v(-99.1, -89.23) * mm, "end": v(-98.59, -89.8) * mm});
            skLineSegment(sketch, "E64.23.3", {"start": v(-98.59, -89.8) * mm, "end": v(-95.76, -87.25) * mm});
            skLineSegment(sketch, "E64.23.4", {"start": v(-96.27, -86.68) * mm, "end": v(-95.76, -87.25) * mm});
            skLineSegment(sketch, "E64.23.5", {"start": v(-96.27, -86.68) * mm, "end": v(-96.78, -86.11) * mm});
            skLineSegment(sketch, "E64.24.0", {"start": v(-89.8, -98.59) * mm, "end": v(-87.25, -95.76) * mm});
            skLineSegment(sketch, "E64.24.1", {"start": v(-89.23, -99.1) * mm, "end": v(-89.8, -98.59) * mm});
            skLineSegment(sketch, "E64.24.2", {"start": v(-89.23, -99.1) * mm, "end": v(-88.66, -99.6) * mm});
            skLineSegment(sketch, "E64.24.3", {"start": v(-88.66, -99.6) * mm, "end": v(-86.11, -96.78) * mm});
            skLineSegment(sketch, "E64.24.4", {"start": v(-86.68, -96.27) * mm, "end": v(-86.11, -96.78) * mm});
            skLineSegment(sketch, "E64.24.5", {"start": v(-86.68, -96.27) * mm, "end": v(-87.25, -95.76) * mm});
            skLineSegment(sketch, "E64.25.0", {"start": v(-79, -107.43) * mm, "end": v(-76.76, -104.35) * mm});
            skLineSegment(sketch, "E64.25.1", {"start": v(-78.38, -107.88) * mm, "end": v(-79, -107.43) * mm});
            skLineSegment(sketch, "E64.25.2", {"start": v(-78.38, -107.88) * mm, "end": v(-77.76, -108.33) * mm});
            skLineSegment(sketch, "E64.25.3", {"start": v(-77.76, -108.33) * mm, "end": v(-75.53, -105.25) * mm});
            skLineSegment(sketch, "E64.25.4", {"start": v(-76.14, -104.8) * mm, "end": v(-75.53, -105.25) * mm});
            skLineSegment(sketch, "E64.25.5", {"start": v(-76.14, -104.8) * mm, "end": v(-76.76, -104.35) * mm});
            skLineSegment(sketch, "E64.27.0", {"start": v(-54.93, -121.51) * mm, "end": v(-53.38, -118.03) * mm});
            skLineSegment(sketch, "E64.27.1", {"start": v(-54.24, -121.82) * mm, "end": v(-54.93, -121.51) * mm});
            skLineSegment(sketch, "E64.27.2", {"start": v(-54.24, -121.82) * mm, "end": v(-53.54, -122.13) * mm});
            skLineSegment(sketch, "E64.27.3", {"start": v(-53.54, -122.13) * mm, "end": v(-52, -118.65) * mm});
            skLineSegment(sketch, "E64.27.4", {"start": v(-52.69, -118.34) * mm, "end": v(-52, -118.65) * mm});
            skLineSegment(sketch, "E64.27.5", {"start": v(-52.69, -118.34) * mm, "end": v(-53.38, -118.03) * mm});
            skLineSegment(sketch, "E64.28.0", {"start": v(-41.93, -126.59) * mm, "end": v(-40.75, -122.96) * mm});
            skLineSegment(sketch, "E64.28.1", {"start": v(-41.2, -126.82) * mm, "end": v(-41.93, -126.59) * mm});
            skLineSegment(sketch, "E64.28.2", {"start": v(-41.2, -126.82) * mm, "end": v(-40.48, -127.06) * mm});
            skLineSegment(sketch, "E64.28.3", {"start": v(-40.48, -127.06) * mm, "end": v(-39.3, -123.44) * mm});
            skLineSegment(sketch, "E64.28.4", {"start": v(-40.03, -123.2) * mm, "end": v(-39.3, -123.44) * mm});
            skLineSegment(sketch, "E64.28.5", {"start": v(-40.03, -123.2) * mm, "end": v(-40.75, -122.96) * mm});
            skLineSegment(sketch, "E64.29.0", {"start": v(-28.47, -130.28) * mm, "end": v(-27.68, -126.55) * mm});
            skLineSegment(sketch, "E64.29.1", {"start": v(-27.73, -130.44) * mm, "end": v(-28.47, -130.28) * mm});
            skLineSegment(sketch, "E64.29.2", {"start": v(-27.73, -130.44) * mm, "end": v(-26.98, -130.6) * mm});
            skLineSegment(sketch, "E64.29.3", {"start": v(-26.98, -130.6) * mm, "end": v(-26.19, -126.87) * mm});
            skLineSegment(sketch, "E64.29.4", {"start": v(-26.93, -126.7) * mm, "end": v(-26.19, -126.87) * mm});
            skLineSegment(sketch, "E64.29.5", {"start": v(-26.93, -126.7) * mm, "end": v(-27.68, -126.55) * mm});
            skLineSegment(sketch, "E64.30.0", {"start": v(-14.7, -132.54) * mm, "end": v(-14.3, -128.75) * mm});
            skLineSegment(sketch, "E64.30.1", {"start": v(-13.94, -132.62) * mm, "end": v(-14.7, -132.54) * mm});
            skLineSegment(sketch, "E64.30.2", {"start": v(-13.94, -132.62) * mm, "end": v(-13.18, -132.7) * mm});
            skLineSegment(sketch, "E64.30.3", {"start": v(-13.18, -132.7) * mm, "end": v(-12.78, -128.91) * mm});
            skLineSegment(sketch, "E64.30.4", {"start": v(-13.54, -128.83) * mm, "end": v(-12.78, -128.91) * mm});
            skLineSegment(sketch, "E64.30.5", {"start": v(-13.54, -128.83) * mm, "end": v(-14.3, -128.75) * mm});
            skLineSegment(sketch, "E64.32.0", {"start": v(13.18, -132.7) * mm, "end": v(12.78, -128.91) * mm});
            skLineSegment(sketch, "E64.32.1", {"start": v(13.94, -132.62) * mm, "end": v(13.18, -132.7) * mm});
            skLineSegment(sketch, "E64.32.2", {"start": v(13.94, -132.62) * mm, "end": v(14.7, -132.54) * mm});
            skLineSegment(sketch, "E64.32.3", {"start": v(14.7, -132.54) * mm, "end": v(14.3, -128.75) * mm});
            skLineSegment(sketch, "E64.32.4", {"start": v(13.54, -128.83) * mm, "end": v(14.3, -128.75) * mm});
            skLineSegment(sketch, "E64.32.5", {"start": v(13.54, -128.83) * mm, "end": v(12.78, -128.91) * mm});
            skLineSegment(sketch, "E64.33.0", {"start": v(26.98, -130.6) * mm, "end": v(26.19, -126.87) * mm});
            skLineSegment(sketch, "E64.33.1", {"start": v(27.73, -130.44) * mm, "end": v(26.98, -130.6) * mm});
            skLineSegment(sketch, "E64.33.2", {"start": v(27.73, -130.44) * mm, "end": v(28.47, -130.28) * mm});
            skLineSegment(sketch, "E64.33.3", {"start": v(28.47, -130.28) * mm, "end": v(27.68, -126.55) * mm});
            skLineSegment(sketch, "E64.33.4", {"start": v(26.93, -126.7) * mm, "end": v(27.68, -126.55) * mm});
            skLineSegment(sketch, "E64.33.5", {"start": v(26.93, -126.7) * mm, "end": v(26.19, -126.87) * mm});
            skLineSegment(sketch, "E64.34.0", {"start": v(40.48, -127.06) * mm, "end": v(39.3, -123.44) * mm});
            skLineSegment(sketch, "E64.34.1", {"start": v(41.2, -126.82) * mm, "end": v(40.48, -127.06) * mm});
            skLineSegment(sketch, "E64.34.2", {"start": v(41.2, -126.82) * mm, "end": v(41.93, -126.59) * mm});
            skLineSegment(sketch, "E64.34.3", {"start": v(41.93, -126.59) * mm, "end": v(40.75, -122.96) * mm});
            skLineSegment(sketch, "E64.34.4", {"start": v(40.03, -123.2) * mm, "end": v(40.75, -122.96) * mm});
            skLineSegment(sketch, "E64.34.5", {"start": v(40.03, -123.2) * mm, "end": v(39.3, -123.44) * mm});
            skLineSegment(sketch, "E64.35.0", {"start": v(53.54, -122.13) * mm, "end": v(52, -118.65) * mm});
            skLineSegment(sketch, "E64.35.1", {"start": v(54.24, -121.82) * mm, "end": v(53.54, -122.13) * mm});
            skLineSegment(sketch, "E64.35.2", {"start": v(54.24, -121.82) * mm, "end": v(54.93, -121.51) * mm});
            skLineSegment(sketch, "E64.35.3", {"start": v(54.93, -121.51) * mm, "end": v(53.38, -118.03) * mm});
            skLineSegment(sketch, "E64.35.4", {"start": v(52.69, -118.34) * mm, "end": v(53.38, -118.03) * mm});
            skLineSegment(sketch, "E64.35.5", {"start": v(52.69, -118.34) * mm, "end": v(52, -118.65) * mm});
            skLineSegment(sketch, "E64.37.0", {"start": v(77.76, -108.33) * mm, "end": v(75.53, -105.25) * mm});
            skLineSegment(sketch, "E64.37.1", {"start": v(78.38, -107.88) * mm, "end": v(77.76, -108.33) * mm});
            skLineSegment(sketch, "E64.37.2", {"start": v(78.38, -107.88) * mm, "end": v(79, -107.43) * mm});
            skLineSegment(sketch, "E64.37.3", {"start": v(79, -107.43) * mm, "end": v(76.76, -104.35) * mm});
            skLineSegment(sketch, "E64.37.4", {"start": v(76.14, -104.8) * mm, "end": v(76.76, -104.35) * mm});
            skLineSegment(sketch, "E64.37.5", {"start": v(76.14, -104.8) * mm, "end": v(75.53, -105.25) * mm});
            skLineSegment(sketch, "E64.38.0", {"start": v(88.66, -99.6) * mm, "end": v(86.11, -96.78) * mm});
            skLineSegment(sketch, "E64.38.1", {"start": v(89.23, -99.1) * mm, "end": v(88.66, -99.6) * mm});
            skLineSegment(sketch, "E64.38.2", {"start": v(89.23, -99.1) * mm, "end": v(89.8, -98.59) * mm});
            skLineSegment(sketch, "E64.38.3", {"start": v(89.8, -98.59) * mm, "end": v(87.25, -95.76) * mm});
            skLineSegment(sketch, "E64.38.4", {"start": v(86.68, -96.27) * mm, "end": v(87.25, -95.76) * mm});
            skLineSegment(sketch, "E64.38.5", {"start": v(86.68, -96.27) * mm, "end": v(86.11, -96.78) * mm});
            skLineSegment(sketch, "E64.39.0", {"start": v(98.59, -89.8) * mm, "end": v(95.76, -87.25) * mm});
            skLineSegment(sketch, "E64.39.1", {"start": v(99.1, -89.23) * mm, "end": v(98.59, -89.8) * mm});
            skLineSegment(sketch, "E64.39.2", {"start": v(99.1, -89.23) * mm, "end": v(99.6, -88.66) * mm});
            skLineSegment(sketch, "E64.39.3", {"start": v(99.6, -88.66) * mm, "end": v(96.78, -86.11) * mm});
            skLineSegment(sketch, "E64.39.4", {"start": v(96.27, -86.68) * mm, "end": v(96.78, -86.11) * mm});
            skLineSegment(sketch, "E64.39.5", {"start": v(96.27, -86.68) * mm, "end": v(95.76, -87.25) * mm});
            skLineSegment(sketch, "E64.40.0", {"start": v(107.43, -79) * mm, "end": v(104.35, -76.76) * mm});
            skLineSegment(sketch, "E64.40.1", {"start": v(107.88, -78.38) * mm, "end": v(107.43, -79) * mm});
            skLineSegment(sketch, "E64.40.2", {"start": v(107.88, -78.38) * mm, "end": v(108.33, -77.76) * mm});
            skLineSegment(sketch, "E64.40.3", {"start": v(108.33, -77.76) * mm, "end": v(105.25, -75.53) * mm});
            skLineSegment(sketch, "E64.40.4", {"start": v(104.8, -76.14) * mm, "end": v(105.25, -75.53) * mm});
            skLineSegment(sketch, "E64.40.5", {"start": v(104.8, -76.14) * mm, "end": v(104.35, -76.76) * mm});
            skLineSegment(sketch, "E64.42.0", {"start": v(121.51, -54.93) * mm, "end": v(118.03, -53.38) * mm});
            skLineSegment(sketch, "E64.42.1", {"start": v(121.82, -54.24) * mm, "end": v(121.51, -54.93) * mm});
            skLineSegment(sketch, "E64.42.2", {"start": v(121.82, -54.24) * mm, "end": v(122.13, -53.54) * mm});
            skLineSegment(sketch, "E64.42.3", {"start": v(122.13, -53.54) * mm, "end": v(118.65, -52) * mm});
            skLineSegment(sketch, "E64.42.4", {"start": v(118.34, -52.69) * mm, "end": v(118.65, -52) * mm});
            skLineSegment(sketch, "E64.42.5", {"start": v(118.34, -52.69) * mm, "end": v(118.03, -53.38) * mm});
            skLineSegment(sketch, "E64.43.0", {"start": v(126.59, -41.93) * mm, "end": v(122.96, -40.75) * mm});
            skLineSegment(sketch, "E64.43.1", {"start": v(126.82, -41.2) * mm, "end": v(126.59, -41.93) * mm});
            skLineSegment(sketch, "E64.43.2", {"start": v(126.82, -41.2) * mm, "end": v(127.06, -40.48) * mm});
            skLineSegment(sketch, "E64.43.3", {"start": v(127.06, -40.48) * mm, "end": v(123.44, -39.3) * mm});
            skLineSegment(sketch, "E64.43.4", {"start": v(123.2, -40.03) * mm, "end": v(123.44, -39.3) * mm});
            skLineSegment(sketch, "E64.43.5", {"start": v(123.2, -40.03) * mm, "end": v(122.96, -40.75) * mm});
            skLineSegment(sketch, "E64.44.0", {"start": v(130.28, -28.47) * mm, "end": v(126.55, -27.68) * mm});
            skLineSegment(sketch, "E64.44.1", {"start": v(130.44, -27.73) * mm, "end": v(130.28, -28.47) * mm});
            skLineSegment(sketch, "E64.44.2", {"start": v(130.44, -27.73) * mm, "end": v(130.6, -26.98) * mm});
            skLineSegment(sketch, "E64.44.3", {"start": v(130.6, -26.98) * mm, "end": v(126.87, -26.19) * mm});
            skLineSegment(sketch, "E64.44.4", {"start": v(126.7, -26.93) * mm, "end": v(126.87, -26.19) * mm});
            skLineSegment(sketch, "E64.44.5", {"start": v(126.7, -26.93) * mm, "end": v(126.55, -27.68) * mm});
            skLineSegment(sketch, "E64.45.0", {"start": v(132.54, -14.7) * mm, "end": v(128.75, -14.3) * mm});
            skLineSegment(sketch, "E64.45.1", {"start": v(132.62, -13.94) * mm, "end": v(132.54, -14.7) * mm});
            skLineSegment(sketch, "E64.45.2", {"start": v(132.62, -13.94) * mm, "end": v(132.7, -13.18) * mm});
            skLineSegment(sketch, "E64.45.3", {"start": v(132.7, -13.18) * mm, "end": v(128.91, -12.78) * mm});
            skLineSegment(sketch, "E64.45.4", {"start": v(128.83, -13.54) * mm, "end": v(128.91, -12.78) * mm});
            skLineSegment(sketch, "E64.45.5", {"start": v(128.83, -13.54) * mm, "end": v(128.75, -14.3) * mm});
            skLineSegment(sketch, "E64.47.0", {"start": v(132.7, 13.18) * mm, "end": v(128.91, 12.78) * mm});
            skLineSegment(sketch, "E64.47.1", {"start": v(132.62, 13.94) * mm, "end": v(132.7, 13.18) * mm});
            skLineSegment(sketch, "E64.47.2", {"start": v(132.62, 13.94) * mm, "end": v(132.54, 14.7) * mm});
            skLineSegment(sketch, "E64.47.3", {"start": v(132.54, 14.7) * mm, "end": v(128.75, 14.3) * mm});
            skLineSegment(sketch, "E64.47.4", {"start": v(128.83, 13.54) * mm, "end": v(128.75, 14.3) * mm});
            skLineSegment(sketch, "E64.47.5", {"start": v(128.83, 13.54) * mm, "end": v(128.91, 12.78) * mm});
            skLineSegment(sketch, "E64.48.0", {"start": v(130.6, 26.98) * mm, "end": v(126.87, 26.19) * mm});
            skLineSegment(sketch, "E64.48.1", {"start": v(130.44, 27.73) * mm, "end": v(130.6, 26.98) * mm});
            skLineSegment(sketch, "E64.48.2", {"start": v(130.44, 27.73) * mm, "end": v(130.28, 28.47) * mm});
            skLineSegment(sketch, "E64.48.3", {"start": v(130.28, 28.47) * mm, "end": v(126.55, 27.68) * mm});
            skLineSegment(sketch, "E64.48.4", {"start": v(126.7, 26.93) * mm, "end": v(126.55, 27.68) * mm});
            skLineSegment(sketch, "E64.48.5", {"start": v(126.7, 26.93) * mm, "end": v(126.87, 26.19) * mm});
            skLineSegment(sketch, "E64.49.0", {"start": v(127.06, 40.48) * mm, "end": v(123.44, 39.3) * mm});
            skLineSegment(sketch, "E64.49.1", {"start": v(126.82, 41.2) * mm, "end": v(127.06, 40.48) * mm});
            skLineSegment(sketch, "E64.49.2", {"start": v(126.82, 41.2) * mm, "end": v(126.59, 41.93) * mm});
            skLineSegment(sketch, "E64.49.3", {"start": v(126.59, 41.93) * mm, "end": v(122.96, 40.75) * mm});
            skLineSegment(sketch, "E64.49.4", {"start": v(123.2, 40.03) * mm, "end": v(122.96, 40.75) * mm});
            skLineSegment(sketch, "E64.49.5", {"start": v(123.2, 40.03) * mm, "end": v(123.44, 39.3) * mm});
            skLineSegment(sketch, "E64.50.0", {"start": v(122.13, 53.54) * mm, "end": v(118.65, 52) * mm});
            skLineSegment(sketch, "E64.50.1", {"start": v(121.82, 54.24) * mm, "end": v(122.13, 53.54) * mm});
            skLineSegment(sketch, "E64.50.2", {"start": v(121.82, 54.24) * mm, "end": v(121.51, 54.93) * mm});
            skLineSegment(sketch, "E64.50.3", {"start": v(121.51, 54.93) * mm, "end": v(118.03, 53.38) * mm});
            skLineSegment(sketch, "E64.50.4", {"start": v(118.34, 52.69) * mm, "end": v(118.03, 53.38) * mm});
            skLineSegment(sketch, "E64.50.5", {"start": v(118.34, 52.69) * mm, "end": v(118.65, 52) * mm});
            skLineSegment(sketch, "E64.52.0", {"start": v(108.33, 77.76) * mm, "end": v(105.25, 75.53) * mm});
            skLineSegment(sketch, "E64.52.1", {"start": v(107.88, 78.38) * mm, "end": v(108.33, 77.76) * mm});
            skLineSegment(sketch, "E64.52.2", {"start": v(107.88, 78.38) * mm, "end": v(107.43, 79) * mm});
            skLineSegment(sketch, "E64.52.3", {"start": v(107.43, 79) * mm, "end": v(104.35, 76.76) * mm});
            skLineSegment(sketch, "E64.52.4", {"start": v(104.8, 76.14) * mm, "end": v(104.35, 76.76) * mm});
            skLineSegment(sketch, "E64.52.5", {"start": v(104.8, 76.14) * mm, "end": v(105.25, 75.53) * mm});
            skLineSegment(sketch, "E64.53.0", {"start": v(99.6, 88.66) * mm, "end": v(96.78, 86.11) * mm});
            skLineSegment(sketch, "E64.53.1", {"start": v(99.1, 89.23) * mm, "end": v(99.6, 88.66) * mm});
            skLineSegment(sketch, "E64.53.2", {"start": v(99.1, 89.23) * mm, "end": v(98.59, 89.8) * mm});
            skLineSegment(sketch, "E64.53.3", {"start": v(98.59, 89.8) * mm, "end": v(95.76, 87.25) * mm});
            skLineSegment(sketch, "E64.53.4", {"start": v(96.27, 86.68) * mm, "end": v(95.76, 87.25) * mm});
            skLineSegment(sketch, "E64.53.5", {"start": v(96.27, 86.68) * mm, "end": v(96.78, 86.11) * mm});
            skLineSegment(sketch, "E64.54.0", {"start": v(89.8, 98.59) * mm, "end": v(87.25, 95.76) * mm});
            skLineSegment(sketch, "E64.54.1", {"start": v(89.23, 99.1) * mm, "end": v(89.8, 98.59) * mm});
            skLineSegment(sketch, "E64.54.2", {"start": v(89.23, 99.1) * mm, "end": v(88.66, 99.6) * mm});
            skLineSegment(sketch, "E64.54.3", {"start": v(88.66, 99.6) * mm, "end": v(86.11, 96.78) * mm});
            skLineSegment(sketch, "E64.54.4", {"start": v(86.68, 96.27) * mm, "end": v(86.11, 96.78) * mm});
            skLineSegment(sketch, "E64.54.5", {"start": v(86.68, 96.27) * mm, "end": v(87.25, 95.76) * mm});
            skLineSegment(sketch, "E64.55.0", {"start": v(79, 107.43) * mm, "end": v(76.76, 104.35) * mm});
            skLineSegment(sketch, "E64.55.1", {"start": v(78.38, 107.88) * mm, "end": v(79, 107.43) * mm});
            skLineSegment(sketch, "E64.55.2", {"start": v(78.38, 107.88) * mm, "end": v(77.76, 108.33) * mm});
            skLineSegment(sketch, "E64.55.3", {"start": v(77.76, 108.33) * mm, "end": v(75.53, 105.25) * mm});
            skLineSegment(sketch, "E64.55.4", {"start": v(76.14, 104.8) * mm, "end": v(75.53, 105.25) * mm});
            skLineSegment(sketch, "E64.55.5", {"start": v(76.14, 104.8) * mm, "end": v(76.76, 104.35) * mm});
            skLineSegment(sketch, "E64.57.0", {"start": v(54.93, 121.51) * mm, "end": v(53.38, 118.03) * mm});
            skLineSegment(sketch, "E64.57.1", {"start": v(54.24, 121.82) * mm, "end": v(54.93, 121.51) * mm});
            skLineSegment(sketch, "E64.57.2", {"start": v(54.24, 121.82) * mm, "end": v(53.54, 122.13) * mm});
            skLineSegment(sketch, "E64.57.3", {"start": v(53.54, 122.13) * mm, "end": v(52, 118.65) * mm});
            skLineSegment(sketch, "E64.57.4", {"start": v(52.69, 118.34) * mm, "end": v(52, 118.65) * mm});
            skLineSegment(sketch, "E64.57.5", {"start": v(52.69, 118.34) * mm, "end": v(53.38, 118.03) * mm});
            skPoint(sketch, "E64.center", {"position": v(0, 0) * mm});
            skLineSegment(sketch, "E65.2.58.0", {"start": v(41.93, 126.59) * mm, "end": v(40.75, 122.96) * mm});
            skLineSegment(sketch, "E65.3.58.0", {"start": v(41.2, 126.82) * mm, "end": v(41.93, 126.59) * mm});
            skLineSegment(sketch, "E65.6.58.0", {"start": v(41.2, 126.82) * mm, "end": v(40.48, 127.06) * mm});
            skLineSegment(sketch, "E65.9.58.0", {"start": v(40.48, 127.06) * mm, "end": v(39.3, 123.44) * mm});
            skLineSegment(sketch, "E65.12.58.0", {"start": v(40.03, 123.2) * mm, "end": v(39.3, 123.44) * mm});
            skLineSegment(sketch, "E65.15.58.0", {"start": v(40.03, 123.2) * mm, "end": v(40.75, 122.96) * mm});
            skLineSegment(sketch, "E65.2.59.0", {"start": v(28.47, 130.28) * mm, "end": v(27.68, 126.55) * mm});
            skLineSegment(sketch, "E65.3.59.0", {"start": v(27.73, 130.44) * mm, "end": v(28.47, 130.28) * mm});
            skLineSegment(sketch, "E65.6.59.0", {"start": v(27.73, 130.44) * mm, "end": v(26.98, 130.6) * mm});
            skLineSegment(sketch, "E65.9.59.0", {"start": v(26.98, 130.6) * mm, "end": v(26.19, 126.87) * mm});
            skLineSegment(sketch, "E65.12.59.0", {"start": v(26.93, 126.7) * mm, "end": v(26.19, 126.87) * mm});
            skLineSegment(sketch, "E65.15.59.0", {"start": v(26.93, 126.7) * mm, "end": v(27.68, 126.55) * mm});
            skSolve(sketch);
        }
        {
            var Q0;
            Q0=qSketchRegion(id+"F25",true);
            extrude(context, id + "F26", {"entities" : qUnion([Q0]), "operationType" : NewBodyOperationType.ADD, "depth" : 2.54 * mm});
        }
    });
